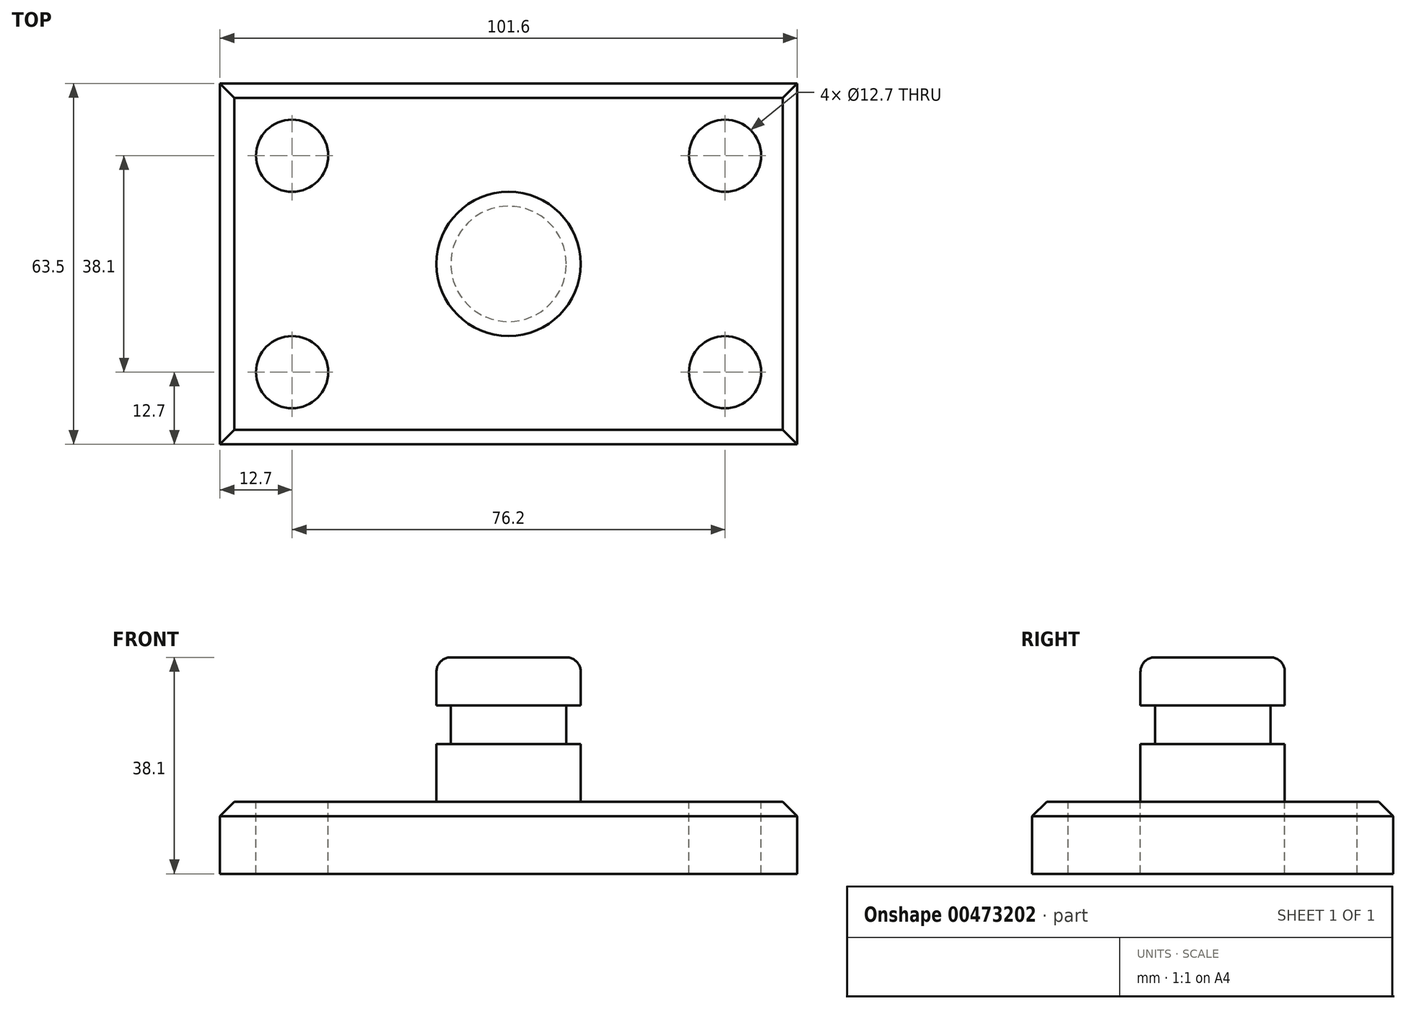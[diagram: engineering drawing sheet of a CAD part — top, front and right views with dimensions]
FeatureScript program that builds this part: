
annotation { "Feature Type Name" : "Feature", "Feature Type Description" : "" }
export const myFeature = defineFeature(function(context is Context, id is Id, definition is map)
    precondition{}
    {
        {
            var Q0;
            Q0=qCreatedBy(makeId("Top.planeOp"),FACE);
            var sketch = newSketch(context, id + "F0", { "sketchPlane" : qUnion([Q0])});
            skLineSegment(sketch, "E0.bottom", {"start": v(-50.8, 31.75) * mm, "end": v(50.8, 31.75) * mm});
            skLineSegment(sketch, "E0.top", {"start": v(-50.8, -31.75) * mm, "end": v(50.8, -31.75) * mm});
            skLineSegment(sketch, "E0.left", {"start": v(-50.8, 31.75) * mm, "end": v(-50.8, -31.75) * mm});
            skLineSegment(sketch, "E0.right", {"start": v(50.8, 31.75) * mm, "end": v(50.8, -31.75) * mm});
            skPoint(sketch, "E0.middle", {"position": v(0, 0) * mm});
            skSolve(sketch);
        }
        {
            var Q0;
            Q0=makeQuery(id+"F0.imprint","IMPRINT",FACE,{"disambiguationData":[TD([[makeQuery(id+"F0.imprint","IMPRINT",EDGE,{"derivedFrom":sQuery(id+"F0.wireOp",EDGE,"E0.bottom")}),-1.0]])]});
            extrude(context, id + "F1", {"entities" : qUnion([Q0]), "depth" : 12.7 * mm});
        }
        {
            var Q0;
            Q0=makeQuery(id+"F1.opExtrude","CAP_FACE",FACE,{"disambiguationData":[OSD([sQuery(id+"F0.wireOp",EDGE,"E0.bottom"),sQuery(id+"F0.wireOp",EDGE,"E0.top"),sQuery(id+"F0.wireOp",EDGE,"E0.left"),sQuery(id+"F0.wireOp",EDGE,"E0.right")])],"isStart":false});
            var sketch = newSketch(context, id + "F2", { "sketchPlane" : qUnion([Q0])});
            skSolve(sketch);
        }
        {
            var Q0;
            Q0=makeQuery(id+"F2.imprint","IMPRINT",FACE,{"disambiguationData":[TD([[makeQuery(id+"F2.imprint","IMPRINT",EDGE,{"derivedFrom":makeQuery(id+"F1.opExtrude","CAP_EDGE",EDGE,{"disambiguationData":[OSD([sQuery(id+"F0.wireOp",EDGE,"E0.bottom")])],"isStart":false})}),-1.0]])]});
            var sketch = newSketch(context, id + "F3", { "sketchPlane" : qUnion([Q0])});
            skCircle(sketch, "E1", {"center": v(-38.1, 19.05) * mm, "radius": 6.35 * mm});
            skCircle(sketch, "E2", {"center": v(-38.1, -19.05) * mm, "radius": 6.35 * mm});
            skCircle(sketch, "E3", {"center": v(38.1, -19.05) * mm, "radius": 6.35 * mm});
            skCircle(sketch, "E4", {"center": v(38.1, 19.05) * mm, "radius": 6.35 * mm});
            skSolve(sketch);
        }
        {
            var Q0;
            Q0=makeQuery(id+"F3.imprint","IMPRINT",FACE,{"disambiguationData":[TD([[makeQuery(id+"F3.imprint","IMPRINT",EDGE,{"derivedFrom":sQuery(id+"F3.wireOp",EDGE,"E1")}),1.0]])]});
            var Q1;
            Q1=makeQuery(id+"F3.imprint","IMPRINT",FACE,{"disambiguationData":[TD([[makeQuery(id+"F3.imprint","IMPRINT",EDGE,{"derivedFrom":sQuery(id+"F3.wireOp",EDGE,"E4")}),1.0]])]});
            var Q2;
            Q2=makeQuery(id+"F3.imprint","IMPRINT",FACE,{"disambiguationData":[TD([[makeQuery(id+"F3.imprint","IMPRINT",EDGE,{"derivedFrom":sQuery(id+"F3.wireOp",EDGE,"E3")}),1.0]])]});
            var Q3;
            Q3=makeQuery(id+"F3.imprint","IMPRINT",FACE,{"disambiguationData":[TD([[makeQuery(id+"F3.imprint","IMPRINT",EDGE,{"derivedFrom":sQuery(id+"F3.wireOp",EDGE,"E2")}),1.0]])]});
            extrude(context, id + "F4", {"entities" : qUnion([Q0, Q1, Q2, Q3]), "operationType" : NewBodyOperationType.REMOVE, "endBound" : BoundingType.THROUGH_ALL, "oppositeDirection" : true, "depth" : 25.4 * mm});
        }
        {
            var Q0;
            Q0=qCreatedBy(makeId("Front.planeOp"),FACE);
            var sketch = newSketch(context, id + "F5", { "sketchPlane" : qUnion([Q0])});
            skLineSegment(sketch, "E5.bottom", {"start": v(0, 12.7) * mm, "end": v(12.7, 12.7) * mm});
            skLineSegment(sketch, "E5.top", {"start": v(0, 38.1) * mm, "end": v(12.7, 38.1) * mm});
            skLineSegment(sketch, "E5.left", {"start": v(0, 12.7) * mm, "end": v(0, 38.1) * mm});
            skLineSegment(sketch, "E5.right", {"start": v(12.7, 12.7) * mm, "end": v(12.7, 38.1) * mm});
            skSolve(sketch);
        }
        {
            var Q0;
            Q0=makeQuery(id+"F5.imprint","IMPRINT",FACE,{"disambiguationData":[TD([[makeQuery(id+"F5.imprint","IMPRINT",EDGE,{"derivedFrom":sQuery(id+"F5.wireOp",EDGE,"E5.bottom")}),1.0]])]});
            var Q1;
            Q1=sQuery(id+"F5.wireOp",EDGE,"E5.left");
            revolve(context, id + "F6", {"operationType" : NewBodyOperationType.ADD, "entities" : qUnion([Q0]), "axis" : qUnion([Q1]), "revolveType" : RevolveType.FULL});
        }
        {
            var Q0;
            Q0=qCreatedBy(makeId("Front.planeOp"),FACE);
            var sketch = newSketch(context, id + "F7", { "sketchPlane" : qUnion([Q0])});
            skLineSegment(sketch, "E6.bottom", {"start": v(10.16, 29.64) * mm, "end": v(21.21, 29.64) * mm});
            skLineSegment(sketch, "E6.top", {"start": v(10.16, 22.86) * mm, "end": v(21.21, 22.86) * mm});
            skLineSegment(sketch, "E6.left", {"start": v(10.16, 29.64) * mm, "end": v(10.16, 22.86) * mm});
            skLineSegment(sketch, "E6.right", {"start": v(21.21, 29.64) * mm, "end": v(21.21, 22.86) * mm});
            skSolve(sketch);
        }
        {
            var Q0;
            Q0=makeQuery(id+"F7.imprint","IMPRINT",FACE,{"disambiguationData":[TD([[makeQuery(id+"F7.imprint","IMPRINT",EDGE,{"derivedFrom":sQuery(id+"F7.wireOp",EDGE,"E6.bottom")}),-1.0]])]});
            var Q1;
            Q1=makeQuery(id+"F6.opRevolve","SWEPT_FACE",FACE,{"disambiguationData":[OSD([sQuery(id+"F5.wireOp",EDGE,"E5.right")])]});
            revolve(context, id + "F8", {"operationType" : NewBodyOperationType.REMOVE, "entities" : qUnion([Q0]), "axis" : qUnion([Q1]), "revolveType" : RevolveType.FULL, "oppositeDirection" : true});
        }
        {
            var Q0;
            Q0=makeQuery(id+"F6.opRevolve","SWEPT_EDGE",EDGE,{"disambiguationData":[OSD([sQuery(id+"F5.wireOp",EDGE,"E5.bottom"),sQuery(id+"F5.wireOp",EDGE,"E5.right")])]});
            var Q1;
            Q1=makeQuery(id+"F6.opRevolve","SWEPT_EDGE",EDGE,{"disambiguationData":[OSD([sQuery(id+"F5.wireOp",EDGE,"E5.top"),sQuery(id+"F5.wireOp",EDGE,"E5.right")])]});
            fillet(context, id + "F9", {"entities" : qUnion([Q0, Q1]), "radius" : 2.54 * mm, "tangentPropagation" : true, "allowEdgeOverflow" : false});
        }
        {
            var Q0;
            Q0=makeQuery(id+"F1.opExtrude","CAP_EDGE",EDGE,{"disambiguationData":[OSD([sQuery(id+"F0.wireOp",EDGE,"E0.top")])],"isStart":false});
            var Q1;
            Q1=makeQuery(id+"F1.opExtrude","CAP_EDGE",EDGE,{"disambiguationData":[OSD([sQuery(id+"F0.wireOp",EDGE,"E0.right")])],"isStart":false});
            var Q2;
            Q2=makeQuery(id+"F1.opExtrude","CAP_EDGE",EDGE,{"disambiguationData":[OSD([sQuery(id+"F0.wireOp",EDGE,"E0.bottom")])],"isStart":false});
            var Q3;
            Q3=makeQuery(id+"F1.opExtrude","CAP_EDGE",EDGE,{"disambiguationData":[OSD([sQuery(id+"F0.wireOp",EDGE,"E0.left")])],"isStart":false});
            chamfer(context, id + "F10", {"entities" : qUnion([Q0, Q1, Q2, Q3]), "width" : 2.54 * mm, "tangentPropagation" : true});
        }
    });
